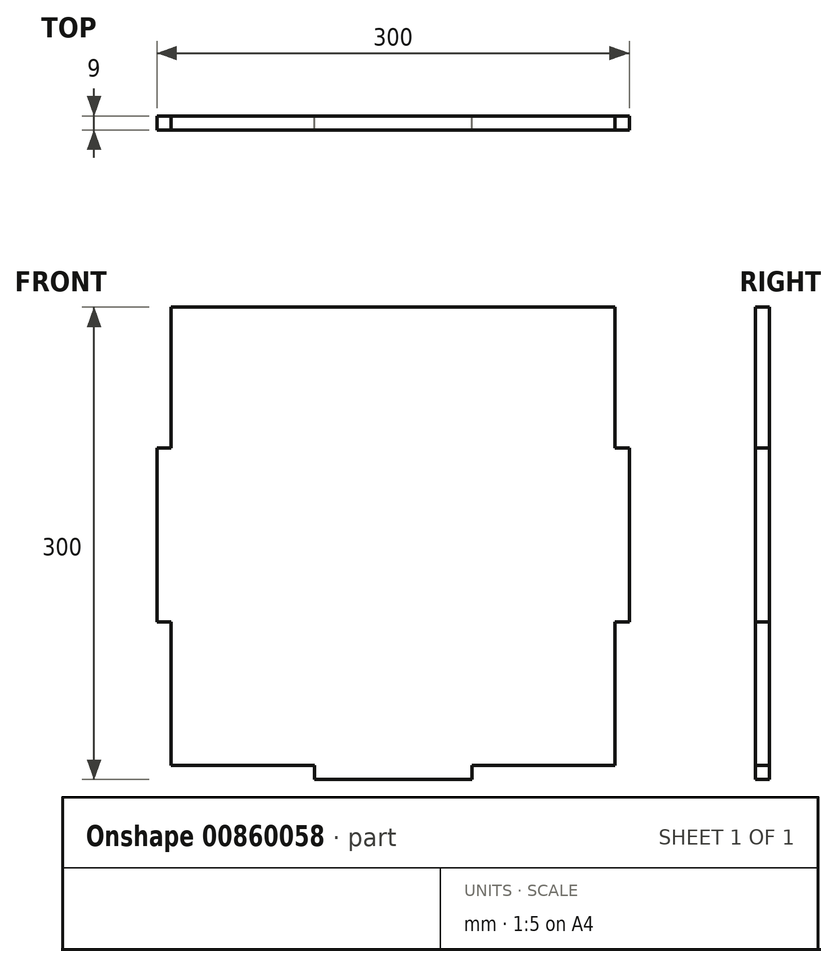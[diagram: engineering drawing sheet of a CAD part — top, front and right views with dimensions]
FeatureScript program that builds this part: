
annotation { "Feature Type Name" : "Feature", "Feature Type Description" : "" }
export const myFeature = defineFeature(function(context is Context, id is Id, definition is map)
    precondition{}
    {
        {
            var Q0;
            Q0=qCreatedBy(makeId("Front.planeOp"),FACE);
            var sketch = newSketch(context, id + "F0", { "sketchPlane" : qUnion([Q0])});
            skLineSegment(sketch, "E0.bottom", {"start": v(150, -150) * mm, "end": v(50, -150) * mm});
            skLineSegment(sketch, "E0.top", {"start": v(150, 150) * mm, "end": v(50, 150) * mm});
            skLineSegment(sketch, "E0.left", {"start": v(150, -150) * mm, "end": v(150, -50) * mm});
            skLineSegment(sketch, "E0.right", {"start": v(-150, -150) * mm, "end": v(-150, -50) * mm});
            skPoint(sketch, "E0.middle", {"position": v(0, 0) * mm});
            skLineSegment(sketch, "E1", {"start": v(-150, -50) * mm, "end": v(-141, -50) * mm});
            skLineSegment(sketch, "E2", {"start": v(-141, -50) * mm, "end": v(-141, 50) * mm});
            skLineSegment(sketch, "E3", {"start": v(-141, 50) * mm, "end": v(-150, 50) * mm});
            skLineSegment(sketch, "E4.trimOffspring", {"start": v(-150, 50) * mm, "end": v(-150, 150) * mm});
            skLineSegment(sketch, "E5", {"start": v(-50, 150) * mm, "end": v(-50, 141) * mm});
            skLineSegment(sketch, "E6", {"start": v(-50, 141) * mm, "end": v(50, 141) * mm});
            skLineSegment(sketch, "E7", {"start": v(50, 141) * mm, "end": v(50, 150) * mm});
            skLineSegment(sketch, "E8", {"start": v(150, 50) * mm, "end": v(141, 50) * mm});
            skLineSegment(sketch, "E9", {"start": v(141, 50) * mm, "end": v(141, -50) * mm});
            skLineSegment(sketch, "E10", {"start": v(141, -50) * mm, "end": v(150, -50) * mm});
            skLineSegment(sketch, "E11", {"start": v(-50, -150) * mm, "end": v(-50, -141) * mm});
            skLineSegment(sketch, "E12", {"start": v(-50, -141) * mm, "end": v(50, -141) * mm});
            skLineSegment(sketch, "E13", {"start": v(50, -141) * mm, "end": v(50, -150) * mm});
            skLineSegment(sketch, "E14.trimOffspring", {"start": v(150, 50) * mm, "end": v(150, 150) * mm});
            skLineSegment(sketch, "E15.trimOffspring", {"start": v(-50, -150) * mm, "end": v(-150, -150) * mm});
            skLineSegment(sketch, "E16", {"start": v(-50, 150) * mm, "end": v(-150, 150) * mm});
            skSolve(sketch);
        }
        {
            var Q0;
            Q0=makeQuery(id+"F0.imprint","IMPRINT",FACE,{"disambiguationData":[TD([[makeQuery(id+"F0.imprint","IMPRINT",EDGE,{"derivedFrom":sQuery(id+"F0.wireOp",EDGE,"E0.bottom")}),-1.0]])]});
            var sketch = newSketch(context, id + "F1", { "sketchPlane" : qUnion([Q0])});
            skLineSegment(sketch, "E17.top", {"start": v(141, 150) * mm, "end": v(-141, 150) * mm});
            skLineSegment(sketch, "E17.left", {"start": v(141, -141) * mm, "end": v(141, -50) * mm});
            skLineSegment(sketch, "E17.right", {"start": v(-141, -141) * mm, "end": v(-141, -50) * mm});
            skPoint(sketch, "E17.middle", {"position": v(0, 0) * mm});
            skLineSegment(sketch, "E18", {"start": v(141, 150) * mm, "end": v(141, 50) * mm});
            skLineSegment(sketch, "E19", {"start": v(141, 50) * mm, "end": v(150, 50) * mm});
            skLineSegment(sketch, "E20", {"start": v(150, 50) * mm, "end": v(150, -50) * mm});
            skLineSegment(sketch, "E21", {"start": v(150, -50) * mm, "end": v(141, -50) * mm});
            skLineSegment(sketch, "E22", {"start": v(-141, 150) * mm, "end": v(-141, 50) * mm});
            skLineSegment(sketch, "E23", {"start": v(-141, 50) * mm, "end": v(-150, 50) * mm});
            skLineSegment(sketch, "E24", {"start": v(-150, 50) * mm, "end": v(-150, -50) * mm});
            skLineSegment(sketch, "E25", {"start": v(-150, -50) * mm, "end": v(-141, -50) * mm});
            skLineSegment(sketch, "E26.trimOffspring", {"start": v(141, 50) * mm, "end": v(141, 150) * mm});
            skLineSegment(sketch, "E27.trimOffspring", {"start": v(-141, 50) * mm, "end": v(-141, 150) * mm});
            skLineSegment(sketch, "E28", {"start": v(-141, -50) * mm, "end": v(-141, -141) * mm});
            skLineSegment(sketch, "E29", {"start": v(-141, -141) * mm, "end": v(-50, -141) * mm});
            skLineSegment(sketch, "E30", {"start": v(-50, -141) * mm, "end": v(-50, -150) * mm});
            skLineSegment(sketch, "E31", {"start": v(50, -150) * mm, "end": v(50, -141) * mm});
            skLineSegment(sketch, "E32", {"start": v(50, -141) * mm, "end": v(141, -141) * mm});
            skPoint(sketch, "E33.orphan", {"position": v(-141, -150) * mm});
            skPoint(sketch, "E34.orphan", {"position": v(141, -150) * mm});
            skLineSegment(sketch, "E35", {"start": v(-50, -150) * mm, "end": v(50, -150) * mm});
            skSolve(sketch);
        }
        {
            var Q0;
            Q0=qCreatedBy(makeId("Right.planeOp"),FACE);
            var sketch = newSketch(context, id + "F2", { "sketchPlane" : qUnion([Q0])});
            skLineSegment(sketch, "E36.bottom", {"start": v(145.5, -150) * mm, "end": v(45.5, -150) * mm});
            skLineSegment(sketch, "E36.top", {"start": v(145.5, 150) * mm, "end": v(45.5, 150) * mm});
            skLineSegment(sketch, "E36.left", {"start": v(145.5, -135) * mm, "end": v(145.5, 150) * mm});
            skLineSegment(sketch, "E36.right", {"start": v(-145.5, -150) * mm, "end": v(-145.5, -50) * mm});
            skPoint(sketch, "E36.middle", {"position": v(0, 0) * mm});
            skLineSegment(sketch, "E37", {"start": v(45.5, 150) * mm, "end": v(45.5, 141) * mm});
            skLineSegment(sketch, "E38", {"start": v(45.5, 141) * mm, "end": v(-54.5, 141) * mm});
            skLineSegment(sketch, "E39", {"start": v(-54.5, 141) * mm, "end": v(-54.5, 150) * mm});
            skLineSegment(sketch, "E40.trimOffspring", {"start": v(-54.5, 150) * mm, "end": v(-145.5, 150) * mm});
            skLineSegment(sketch, "E41", {"start": v(130.5, -150) * mm, "end": v(45.5, -150) * mm});
            skLineSegment(sketch, "E42", {"start": v(45.5, -150) * mm, "end": v(45.5, -141) * mm});
            skLineSegment(sketch, "E43", {"start": v(45.5, -141) * mm, "end": v(-54.5, -141) * mm});
            skLineSegment(sketch, "E44", {"start": v(-54.5, -141) * mm, "end": v(-54.5, -150) * mm});
            skLineSegment(sketch, "E45", {"start": v(-145.5, 50) * mm, "end": v(-154.5, 50) * mm});
            skLineSegment(sketch, "E46", {"start": v(-154.5, 50) * mm, "end": v(-154.5, -50) * mm});
            skLineSegment(sketch, "E47", {"start": v(-154.5, -50) * mm, "end": v(-145.5, -50) * mm});
            skLineSegment(sketch, "E48.trimOffspring", {"start": v(-54.5, -150) * mm, "end": v(-145.5, -150) * mm});
            skLineSegment(sketch, "E49.trimOffspring", {"start": v(-145.5, 50) * mm, "end": v(-145.5, 150) * mm});
            skLineSegment(sketch, "E50", {"start": v(145.5, 150) * mm, "end": v(145.5, 125) * mm});
            skLineSegment(sketch, "E51", {"start": v(145.5, 125) * mm, "end": v(120.5, 125) * mm});
            skCircle(sketch, "E52", {"center": v(120.5, 125) * mm, "radius": 7.5 * mm});
            skPoint(sketch, "E53.visualSharp", {"position": v(145.5, -150) * mm});
            skArc(sketch, "E53.filletArc", {"start": v(130.5, -150) * mm, "mid": v(141.1, -145.6) * mm, "end": v(145.5, -135) * mm});
            skSolve(sketch);
        }
        {
            var Q0;
            Q0=qCreatedBy(makeId("Top.planeOp"),FACE);
            var sketch = newSketch(context, id + "F3", { "sketchPlane" : qUnion([Q0])});
            skLineSegment(sketch, "E54.bottom", {"start": v(140, -140) * mm, "end": v(60, -140) * mm});
            skLineSegment(sketch, "E54.top", {"start": v(140, 140) * mm, "end": v(-140, 140) * mm});
            skLineSegment(sketch, "E54.left", {"start": v(140, -140) * mm, "end": v(140, 131) * mm});
            skLineSegment(sketch, "E54.right", {"start": v(-140, -140) * mm, "end": v(-140, 131) * mm});
            skPoint(sketch, "E54.middle", {"position": v(0, 0) * mm});
            skLineSegment(sketch, "E55", {"start": v(140, 140) * mm, "end": v(149, 140) * mm});
            skLineSegment(sketch, "E56", {"start": v(149, 140) * mm, "end": v(149, 131) * mm});
            skLineSegment(sketch, "E57", {"start": v(149, 131) * mm, "end": v(140, 131) * mm});
            skLineSegment(sketch, "E58", {"start": v(-140, 140) * mm, "end": v(-149, 140) * mm});
            skLineSegment(sketch, "E59", {"start": v(-149, 140) * mm, "end": v(-149, 131) * mm});
            skLineSegment(sketch, "E60", {"start": v(-149, 131) * mm, "end": v(-140, 131) * mm});
            skLineSegment(sketch, "E61", {"start": v(-140, -140) * mm, "end": v(-60, -140) * mm});
            skLineSegment(sketch, "E62", {"start": v(-60, -140) * mm, "end": v(-60, -141) * mm});
            skLineSegment(sketch, "E63", {"start": v(-41, -160) * mm, "end": v(41, -160) * mm});
            skLineSegment(sketch, "E64", {"start": v(60, -141) * mm, "end": v(60, -140) * mm});
            skPoint(sketch, "E65.visualSharp", {"position": v(-60, -160) * mm});
            skArc(sketch, "E65.filletArc", {"start": v(-60, -141) * mm, "mid": v(-54.44, -154.44) * mm, "end": v(-41, -160) * mm});
            skPoint(sketch, "E66.visualSharp", {"position": v(60, -160) * mm});
            skArc(sketch, "E66.filletArc", {"start": v(41, -160) * mm, "mid": v(54.44, -154.44) * mm, "end": v(60, -141) * mm});
            skLineSegment(sketch, "E67.trimOffspring", {"start": v(-60, -140) * mm, "end": v(-140, -140) * mm});
            skSolve(sketch);
        }
        {
            var Q0;
            Q0=qCreatedBy(makeId("Front.planeOp"),FACE);
            var sketch = newSketch(context, id + "F4", { "sketchPlane" : qUnion([Q0])});
            skLineSegment(sketch, "E68.bottom", {"start": v(141, -130.5) * mm, "end": v(50, -130.5) * mm});
            skLineSegment(sketch, "E68.top", {"start": v(141, 130.5) * mm, "end": v(-141, 130.5) * mm});
            skLineSegment(sketch, "E68.left", {"start": v(141, -130.5) * mm, "end": v(141, -39.5) * mm});
            skLineSegment(sketch, "E68.right", {"start": v(-141, -130.5) * mm, "end": v(-141, -39.5) * mm});
            skPoint(sketch, "E68.middle", {"position": v(0, 0) * mm});
            skLineSegment(sketch, "E69", {"start": v(-141, -130.5) * mm, "end": v(-50, -130.5) * mm});
            skLineSegment(sketch, "E70", {"start": v(-50, -130.5) * mm, "end": v(-50, -139.5) * mm});
            skLineSegment(sketch, "E71", {"start": v(-50, -139.5) * mm, "end": v(50, -139.5) * mm});
            skLineSegment(sketch, "E72", {"start": v(50, -139.5) * mm, "end": v(50, -130.5) * mm});
            skLineSegment(sketch, "E73.trimOffspring", {"start": v(-50, -130.5) * mm, "end": v(-141, -130.5) * mm});
            skLineSegment(sketch, "E74", {"start": v(-141, -39.5) * mm, "end": v(-150, -39.5) * mm});
            skLineSegment(sketch, "E75", {"start": v(-150, -39.5) * mm, "end": v(-150, 60.5) * mm});
            skLineSegment(sketch, "E76", {"start": v(-150, 60.5) * mm, "end": v(-141, 60.5) * mm});
            skLineSegment(sketch, "E77.trimOffspring", {"start": v(-141, 60.5) * mm, "end": v(-141, 130.5) * mm});
            skLineSegment(sketch, "E78", {"start": v(141, -39.5) * mm, "end": v(150, -39.5) * mm});
            skLineSegment(sketch, "E79", {"start": v(150, -39.5) * mm, "end": v(150, 60.5) * mm});
            skLineSegment(sketch, "E80", {"start": v(150, 60.5) * mm, "end": v(141, 60.5) * mm});
            skLineSegment(sketch, "E81.trimOffspring", {"start": v(141, 60.5) * mm, "end": v(141, 130.5) * mm});
            skSolve(sketch);
        }
        {
            var Q0;
            Q0 = qSketchRegion(id + "F4", true);
            extrude(context, id + "F5", {"entities" : qUnion([Q0]), "depth" : 9 * mm, "offsetDistance" : 25 * mm});
        }
        {
            var Q0;
            Q0 = qSketchRegion(id + "F1", true);
            extrude(context, id + "F6", {"entities" : qUnion([Q0]), "operationType" : NewBodyOperationType.ADD, "depth" : 9 * mm, "offsetDistance" : 25 * mm});
        }
    });
